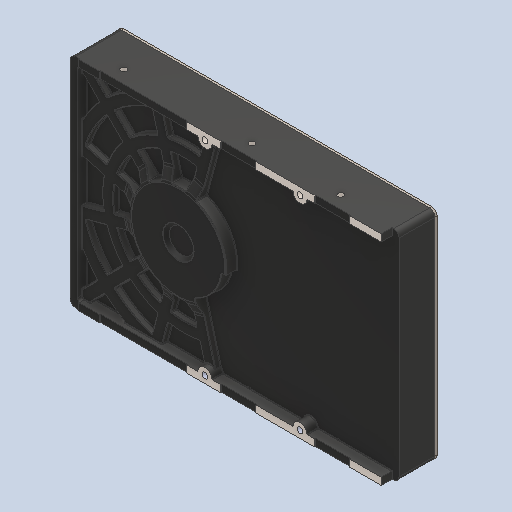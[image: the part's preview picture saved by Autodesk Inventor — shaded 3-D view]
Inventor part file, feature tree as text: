
AUTODESK INVENTOR PART (.ipt)
format: ipt  version: 2023 (Build 270158000, 158)  size: 1,468,416 bytes
history: native  units: mm
features: fillet x1, other x1
ambient origin geometry x8: Origin, YZ Plane, XZ Plane, XY Plane, X Axis, Y Axis, Z Axis, Center Point
bodies: Solid1 (feature_tree), Solid2 (feature_tree)
feature tree (2):
  fillet  "Fillet10"  [1 undecoded]
  other  "Cut-Extrude9"
note: 1 required parameter value undecoded (feature->parameter linkage not recoverable at this tier; creation-order binding heuristic only, values carry confidence <= 0.55)
